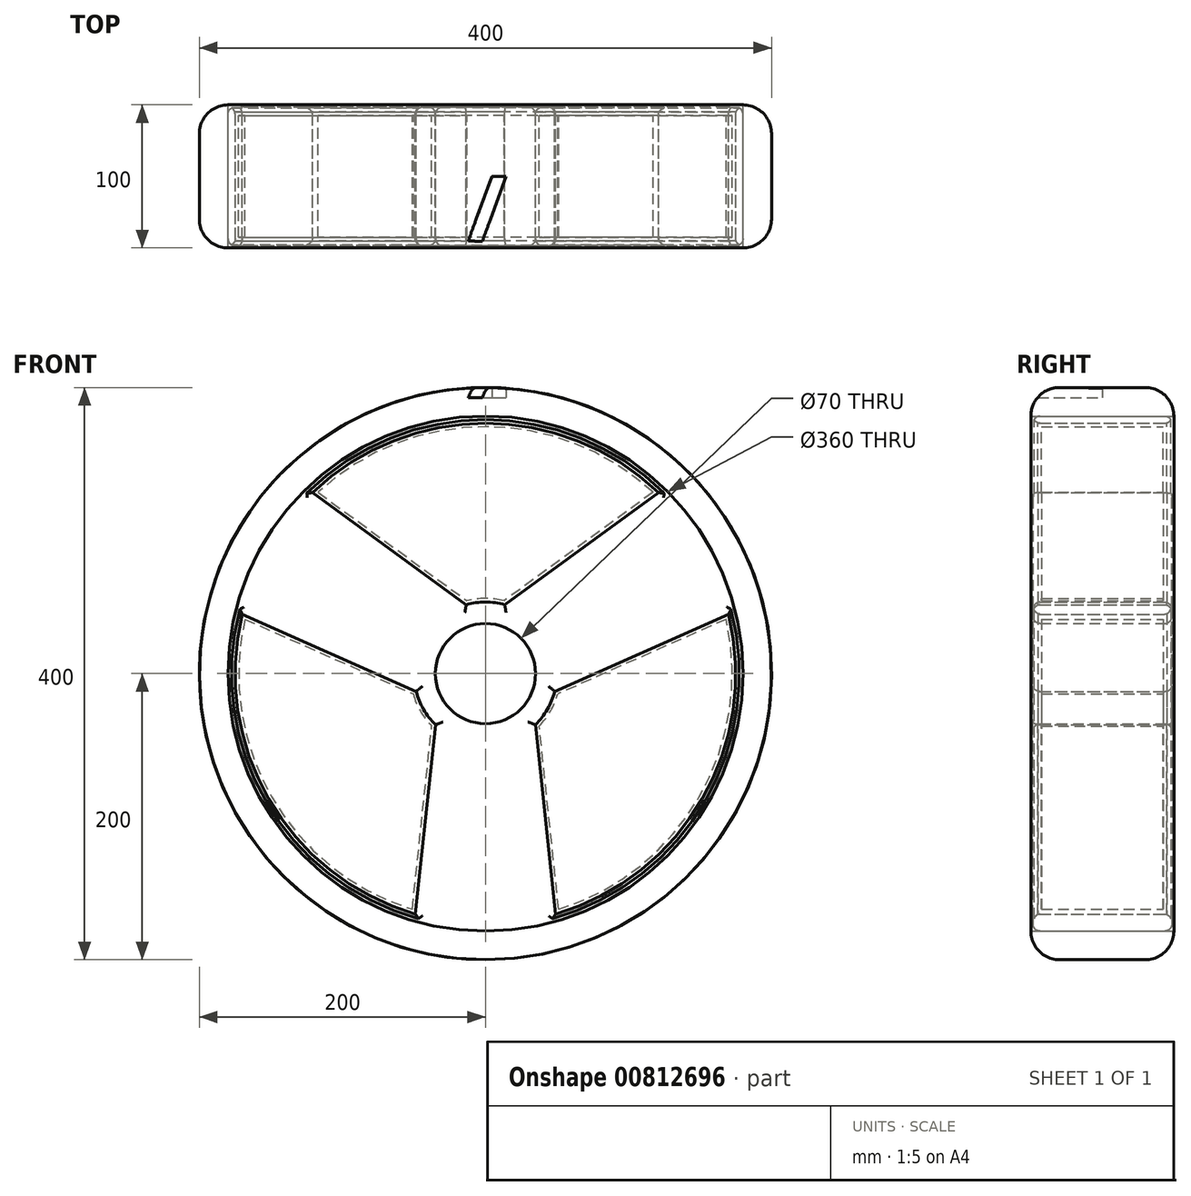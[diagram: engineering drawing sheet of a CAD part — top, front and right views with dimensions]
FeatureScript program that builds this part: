
annotation { "Feature Type Name" : "Feature", "Feature Type Description" : "" }
export const myFeature = defineFeature(function(context is Context, id is Id, definition is map)
    precondition{}
    {
        {
            var Q0;
            Q0=qCreatedBy(makeId("Front.planeOp"),FACE);
            var sketch = newSketch(context, id + "F0", { "sketchPlane" : qUnion([Q0])});
            skCircle(sketch, "E0", {"center": v(0, 0) * mm, "radius": 200 * mm});
            skArc(sketch, "E1", {"start": v(-169.99, 41.57) * mm, "mid": v(-151.55, -87.5) * mm, "end": v(-49, -168) * mm});
            skArc(sketch, "E2", {"start": v(-48.43, -12.42) * mm, "mid": v(-43.3, -25) * mm, "end": v(-34.98, -35.73) * mm});
            skLineSegment(sketch, "E3", {"start": v(-121, 126.43) * mm, "end": v(-13.46, 48.16) * mm});
            skLineSegment(sketch, "E4.MirrorCS", {"start": v(121, 126.43) * mm, "end": v(13.46, 48.16) * mm});
            skLineSegment(sketch, "E5.1.0", {"start": v(-49, -168) * mm, "end": v(-34.98, -35.73) * mm});
            skLineSegment(sketch, "E5.1.1", {"start": v(-169.99, 41.57) * mm, "end": v(-48.43, -12.42) * mm});
            skLineSegment(sketch, "E5.2.0", {"start": v(169.99, 41.57) * mm, "end": v(48.43, -12.42) * mm});
            skLineSegment(sketch, "E5.2.1", {"start": v(49, -168) * mm, "end": v(34.98, -35.73) * mm});
            skArc(sketch, "E6.trimOffspring", {"start": v(13.46, 48.16) * mm, "mid": v(0, 50) * mm, "end": v(-13.46, 48.16) * mm});
            skArc(sketch, "E7.trimOffspring", {"start": v(34.98, -35.73) * mm, "mid": v(43.3, -25) * mm, "end": v(48.43, -12.42) * mm});
            skCircle(sketch, "E8", {"center": v(0, 0) * mm, "radius": 180 * mm});
            skArc(sketch, "E9.trimOffspring", {"start": v(121, 126.43) * mm, "mid": v(0, 175) * mm, "end": v(-121, 126.43) * mm});
            skArc(sketch, "E10.trimOffspring", {"start": v(49, -168) * mm, "mid": v(151.55, -87.5) * mm, "end": v(169.99, 41.57) * mm});
            skCircle(sketch, "E11", {"center": v(0, 0) * mm, "radius": 35 * mm});
            skSolve(sketch);
        }
        {
            var Q0;
            Q0=makeQuery(id+"F0.imprint","IMPRINT",FACE,{"disambiguationData":[TD([[makeQuery(id+"F0.imprint","IMPRINT",EDGE,{"derivedFrom":sQuery(id+"F0.wireOp",EDGE,"E0")}),1.0]])]});
            extrude(context, id + "F1", {"entities" : qUnion([Q0]), "endBound" : BoundingType.SYMMETRIC, "depth" : 100 * mm, "offsetDistance" : 25 * mm});
        }
        {
            var Q0;
            Q0=makeQuery(id+"F0.imprint","IMPRINT",FACE,{"disambiguationData":[TD([[makeQuery(id+"F0.imprint","IMPRINT",EDGE,{"derivedFrom":sQuery(id+"F0.wireOp",EDGE,"E1")}),-1.0]])]});
            extrude(context, id + "F2", {"entities" : qUnion([Q0]), "endBound" : BoundingType.SYMMETRIC, "depth" : 97 * mm, "offsetDistance" : 25 * mm});
        }
        {
            var Q0;
            Q0=makeQuery(id+"F0.imprint","IMPRINT",FACE,{"disambiguationData":[TD([[makeQuery(id+"F0.imprint","IMPRINT",EDGE,{"derivedFrom":sQuery(id+"F0.wireOp",EDGE,"E5.2.0")}),1.0]])]});
            var Q1;
            Q1=makeQuery(id+"F0.imprint","IMPRINT",FACE,{"disambiguationData":[TD([[makeQuery(id+"F0.imprint","IMPRINT",EDGE,{"derivedFrom":sQuery(id+"F0.wireOp",EDGE,"E3")}),1.0]])]});
            var Q2;
            Q2=makeQuery(id+"F0.imprint","IMPRINT",FACE,{"disambiguationData":[TD([[makeQuery(id+"F0.imprint","IMPRINT",EDGE,{"derivedFrom":sQuery(id+"F0.wireOp",EDGE,"E1")}),1.0]])]});
            extrude(context, id + "F3", {"entities" : qUnion([Q0, Q1, Q2]), "endBound" : BoundingType.SYMMETRIC, "depth" : 90 * mm, "offsetDistance" : 25 * mm});
        }
        {
            var Q0;
            Q0=makeQuery(id+"F1.opExtrude","SWEPT_FACE",FACE,{"disambiguationData":[OSD([sQuery(id+"F0.wireOp",EDGE,"E0")])]});
            fillet(context, id + "F4", {"entities" : qUnion([Q0]), "radius" : 20 * mm, "tangentPropagation" : true, "allowEdgeOverflow" : false});
        }
        {
            var Q0;
            Q0=qCreatedBy(makeId("Front.planeOp"),FACE);
            cPlane(context, id + "F5", {"entities" : qUnion([Q0]), "cplaneType" : CPlaneType.OFFSET, "offset" : 50 * mm, "width" : 150 * mm, "height" : 150 * mm});
        }
        {
            var Q0;
            Q0=qCreatedBy(id+"F5.planeOp",FACE);
            var sketch = newSketch(context, id + "F6", { "sketchPlane" : qUnion([Q0])});
            skLineSegment(sketch, "E12.bottom", {"start": v(-13.89, 207.8) * mm, "end": v(-3.89, 207.8) * mm});
            skLineSegment(sketch, "E12.top", {"start": v(-13.89, 192.8) * mm, "end": v(-3.89, 192.8) * mm});
            skLineSegment(sketch, "E12.left", {"start": v(-13.89, 207.8) * mm, "end": v(-13.89, 192.8) * mm});
            skLineSegment(sketch, "E12.right", {"start": v(-3.89, 207.8) * mm, "end": v(-3.89, 192.8) * mm});
            skSolve(sketch);
        }
        {
            var Q0;
            Q0=qCreatedBy(makeId("Front.planeOp"),FACE);
            var sketch = newSketch(context, id + "F7", { "sketchPlane" : qUnion([Q0])});
            skLineSegment(sketch, "E13.bottom", {"start": v(4.46, 207.8) * mm, "end": v(14.46, 207.8) * mm});
            skLineSegment(sketch, "E13.top", {"start": v(4.46, 192.8) * mm, "end": v(14.46, 192.8) * mm});
            skLineSegment(sketch, "E13.left", {"start": v(4.46, 207.8) * mm, "end": v(4.46, 192.8) * mm});
            skLineSegment(sketch, "E13.right", {"start": v(14.46, 207.8) * mm, "end": v(14.46, 192.8) * mm});
            skSolve(sketch);
        }
        {
            var Q1;
            Q1 = qSketchRegion(id + "F6", true);
            var Q2;
            Q2 = qSketchRegion(id + "F7", true);
            loft(context, id + "F8", {"operationType" : NewBodyOperationType.REMOVE, "sheetProfilesArray" : [{ "sheetProfileEntities" : qUnion([Q1]) }, { "sheetProfileEntities" : qUnion([Q2]) }]});
        }
        {
            var Q0;
            Q0=qCreatedBy(makeId("Right.planeOp"),FACE);
            var sketch = newSketch(context, id + "F9", { "sketchPlane" : qUnion([Q0])});
            skLineSegment(sketch, "E14", {"start": v(-148.84, -0.33) * mm, "end": v(190.13, -0.33) * mm});
            skSolve(sketch);
        }
        {
            var Q0;
            Q0=makeQuery(id+"F2.opExtrude","CAP_FACE",FACE,{"disambiguationData":[OSD([sQuery(id+"F0.wireOp",EDGE,"E1"),sQuery(id+"F0.wireOp",EDGE,"E2"),sQuery(id+"F0.wireOp",EDGE,"E3"),sQuery(id+"F0.wireOp",EDGE,"E4.MirrorCS"),sQuery(id+"F0.wireOp",EDGE,"E5.1.0"),sQuery(id+"F0.wireOp",EDGE,"E5.1.1"),sQuery(id+"F0.wireOp",EDGE,"E5.2.0"),sQuery(id+"F0.wireOp",EDGE,"E5.2.1"),sQuery(id+"F0.wireOp",EDGE,"E6.trimOffspring"),sQuery(id+"F0.wireOp",EDGE,"E7.trimOffspring"),sQuery(id+"F0.wireOp",EDGE,"E8"),sQuery(id+"F0.wireOp",EDGE,"E9.trimOffspring"),sQuery(id+"F0.wireOp",EDGE,"E10.trimOffspring"),sQuery(id+"F0.wireOp",EDGE,"E11")])],"isStart":false});
            var Q1;
            Q1=makeQuery(id+"F2.opExtrude","CAP_FACE",FACE,{"disambiguationData":[OSD([sQuery(id+"F0.wireOp",EDGE,"E1"),sQuery(id+"F0.wireOp",EDGE,"E2"),sQuery(id+"F0.wireOp",EDGE,"E3"),sQuery(id+"F0.wireOp",EDGE,"E4.MirrorCS"),sQuery(id+"F0.wireOp",EDGE,"E5.1.0"),sQuery(id+"F0.wireOp",EDGE,"E5.1.1"),sQuery(id+"F0.wireOp",EDGE,"E5.2.0"),sQuery(id+"F0.wireOp",EDGE,"E5.2.1"),sQuery(id+"F0.wireOp",EDGE,"E6.trimOffspring"),sQuery(id+"F0.wireOp",EDGE,"E7.trimOffspring"),sQuery(id+"F0.wireOp",EDGE,"E8"),sQuery(id+"F0.wireOp",EDGE,"E9.trimOffspring"),sQuery(id+"F0.wireOp",EDGE,"E10.trimOffspring"),sQuery(id+"F0.wireOp",EDGE,"E11")])],"isStart":true});
            fillet(context, id + "F10", {"entities" : qUnion([Q0, Q1]), "radius" : 5 * mm, "tangentPropagation" : true, "allowEdgeOverflow" : false});
        }
        {
            var Q0;
            Q0=makeQuery(id+"F3.opExtrude","CAP_FACE",FACE,{"disambiguationData":[OSD([sQuery(id+"F0.wireOp",EDGE,"E5.2.0"),sQuery(id+"F0.wireOp",EDGE,"E5.2.1"),sQuery(id+"F0.wireOp",EDGE,"E7.trimOffspring"),sQuery(id+"F0.wireOp",EDGE,"E10.trimOffspring")])],"isStart":false});
            var Q1;
            Q1=makeQuery(id+"F3.opExtrude","CAP_FACE",FACE,{"disambiguationData":[OSD([sQuery(id+"F0.wireOp",EDGE,"E1"),sQuery(id+"F0.wireOp",EDGE,"E2"),sQuery(id+"F0.wireOp",EDGE,"E5.1.0"),sQuery(id+"F0.wireOp",EDGE,"E5.1.1")])],"isStart":false});
            var Q2;
            Q2=makeQuery(id+"F3.opExtrude","CAP_FACE",FACE,{"disambiguationData":[OSD([sQuery(id+"F0.wireOp",EDGE,"E3"),sQuery(id+"F0.wireOp",EDGE,"E4.MirrorCS"),sQuery(id+"F0.wireOp",EDGE,"E6.trimOffspring"),sQuery(id+"F0.wireOp",EDGE,"E9.trimOffspring")])],"isStart":false});
            var Q3;
            Q3=makeQuery(id+"F3.opExtrude","SWEPT_BODY",BODY,{"disambiguationData":[OSD([sQuery(id+"F0.wireOp",EDGE,"E1"),sQuery(id+"F0.wireOp",EDGE,"E2"),sQuery(id+"F0.wireOp",EDGE,"E5.1.0"),sQuery(id+"F0.wireOp",EDGE,"E5.1.1")])]});
            var Q4;
            Q4=makeQuery(id+"F3.opExtrude","SWEPT_BODY",BODY,{"disambiguationData":[OSD([sQuery(id+"F0.wireOp",EDGE,"E3"),sQuery(id+"F0.wireOp",EDGE,"E4.MirrorCS"),sQuery(id+"F0.wireOp",EDGE,"E6.trimOffspring"),sQuery(id+"F0.wireOp",EDGE,"E9.trimOffspring")])]});
            var Q5;
            Q5=makeQuery(id+"F3.opExtrude","SWEPT_BODY",BODY,{"disambiguationData":[OSD([sQuery(id+"F0.wireOp",EDGE,"E5.2.0"),sQuery(id+"F0.wireOp",EDGE,"E5.2.1"),sQuery(id+"F0.wireOp",EDGE,"E7.trimOffspring"),sQuery(id+"F0.wireOp",EDGE,"E10.trimOffspring")])]});
            shell(context, id + "F11", {"isHollow" : true, "entities" : qUnion([Q0, Q1, Q2]), "parts" : qUnion([Q3, Q4, Q5]), "thickness" : 2.5 * mm});
        }
    });
